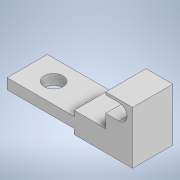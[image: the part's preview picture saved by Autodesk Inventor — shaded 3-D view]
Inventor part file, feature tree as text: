
AUTODESK INVENTOR PART (.ipt)
format: ipt  version: 2020.2 (Build 242310000, 310)  size: 139,264 bytes
history: native  units: mm
features: sketch x5, extrude x4, hole x1
ambient origin geometry x8: Origin, YZ Plane, XZ Plane, XY Plane, X Axis, Y Axis, Z Axis, Center Point
bodies: Solid1 (feature_tree)
feature tree (10):
  extrude  "Extrusion1"  Depth=7.62mm
  extrude  "Extrusion2"  Depth=1.9812mm
  extrude  "Extrusion3"  Depth=11.049mm TaperAngle=0.0deg
  extrude  "Extrusion4"  Depth=5.9944mm TaperAngle=0.0deg
  hole  "Hole1"  [1 undecoded]
  sketch  "Sketch1"  dims[d0=23.749mm d1=7.62mm]
  sketch  "Sketch2"  dims[d2=1.9812mm d3=0.0mm d4=1.9939mm]
  sketch  "Sketch3"  dims[d5=3.9878mm d6=11.049mm d7=0.0mm]
  sketch  "Sketch4"  dims[d8=5.08mm d9=5.9944mm d10=0.0mm]
  sketch  "Sketch5"  dims[d11=1.994mm d12=2.541mm d13=3.0mm d14=10.0mm d15=0.0mm d16=5.0mm d17=3.6mm d18=6.0mm d19=6.3mm d20=2.0mm d21=90.0deg d22=8.0mm d23=20.594885mm]
note: 1 required parameter value undecoded (feature->parameter linkage not recoverable at this tier; creation-order binding heuristic only, values carry confidence <= 0.55)
